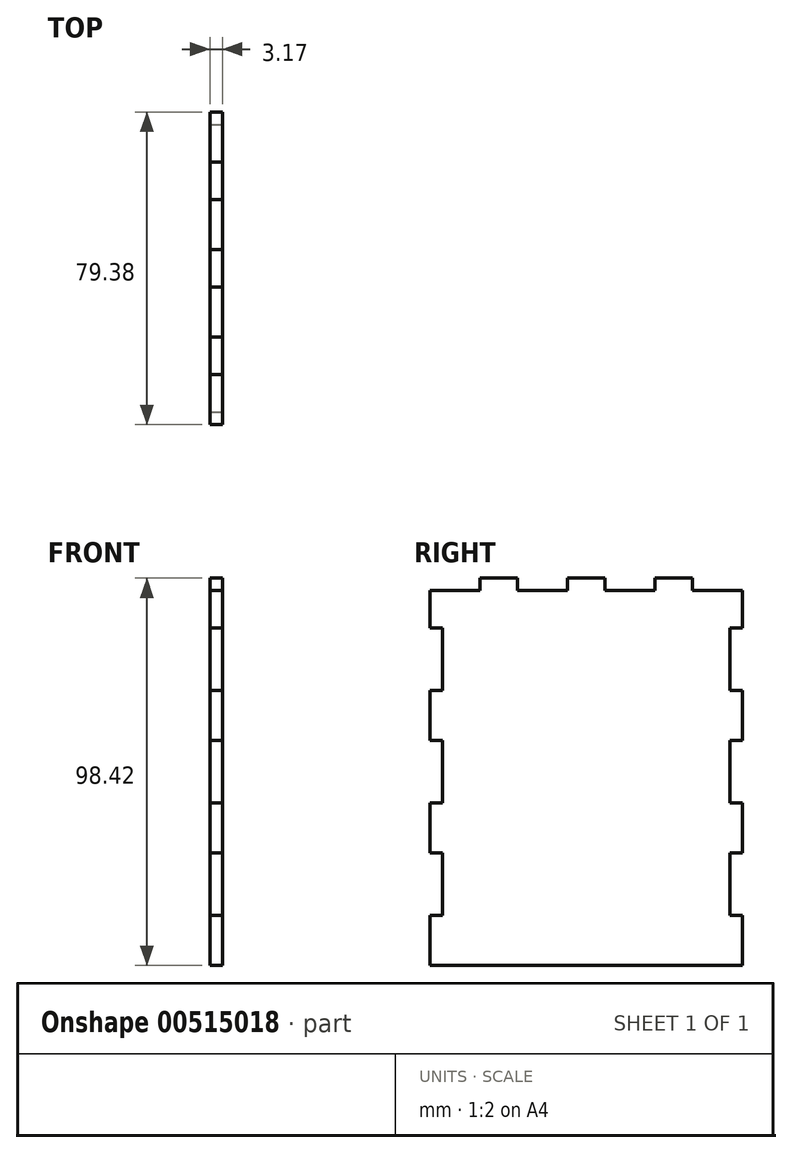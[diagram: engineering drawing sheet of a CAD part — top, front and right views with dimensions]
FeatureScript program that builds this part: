
annotation { "Feature Type Name" : "Feature", "Feature Type Description" : "" }
export const myFeature = defineFeature(function(context is Context, id is Id, definition is map)
    precondition{}
    {
        {
            var Q0;
            Q0=qCreatedBy(makeId("Right.planeOp"),FACE);
            var sketch = newSketch(context, id + "F0", { "sketchPlane" : qUnion([Q0])});
            skLineSegment(sketch, "E0.bottom", {"start": v(-39.69, 49.21) * mm, "end": v(39.69, 49.21) * mm});
            skLineSegment(sketch, "E0.top", {"start": v(-39.69, -49.21) * mm, "end": v(39.69, -49.21) * mm});
            skLineSegment(sketch, "E0.left", {"start": v(-39.69, 49.21) * mm, "end": v(-39.69, -49.21) * mm});
            skLineSegment(sketch, "E0.right", {"start": v(39.69, 49.21) * mm, "end": v(39.69, -49.21) * mm});
            skSolve(sketch);
        }
        {
            var Q0;
            Q0 = qSketchRegion(id + "F0", true);
            extrude(context, id + "F1", {"entities" : qUnion([Q0]), "depth" : 3.17 * mm, "offsetDistance" : 25.4 * mm});
        }
        {
            var Q0;
            Q0=makeQuery(id+"F1.opExtrude","CAP_FACE",FACE,{"disambiguationData":[OSD([sQuery(id+"F0.wireOp",EDGE,"E0.bottom"),sQuery(id+"F0.wireOp",EDGE,"E0.top"),sQuery(id+"F0.wireOp",EDGE,"E0.left"),sQuery(id+"F0.wireOp",EDGE,"E0.right")])],"isStart":false});
            var sketch = newSketch(context, id + "F2", { "sketchPlane" : qUnion([Q0])});
            skLineSegment(sketch, "E1", {"start": v(0, 49.21) * mm, "end": v(0, -49.21) * mm, "construction": true});
            skLineSegment(sketch, "E2.bottom", {"start": v(-39.69, 36.51) * mm, "end": v(-36.51, 36.51) * mm});
            skLineSegment(sketch, "E2.top", {"start": v(-39.69, 20.64) * mm, "end": v(-36.51, 20.64) * mm});
            skLineSegment(sketch, "E2.left", {"start": v(-39.69, 36.51) * mm, "end": v(-39.69, 20.64) * mm});
            skLineSegment(sketch, "E2.right", {"start": v(-36.51, 36.51) * mm, "end": v(-36.51, 20.64) * mm});
            skLineSegment(sketch, "E3.0.1.0", {"start": v(-39.69, -7.94) * mm, "end": v(-36.51, -7.94) * mm});
            skLineSegment(sketch, "E3.0.1.1", {"start": v(-39.69, 7.94) * mm, "end": v(-39.69, -7.94) * mm});
            skLineSegment(sketch, "E3.0.1.2", {"start": v(-39.69, 7.94) * mm, "end": v(-36.51, 7.94) * mm});
            skLineSegment(sketch, "E3.0.1.3", {"start": v(-36.51, 7.94) * mm, "end": v(-36.51, -7.94) * mm});
            skLineSegment(sketch, "E3.0.2.0", {"start": v(-39.69, -36.51) * mm, "end": v(-36.51, -36.51) * mm});
            skLineSegment(sketch, "E3.0.2.1", {"start": v(-39.69, -20.64) * mm, "end": v(-39.69, -36.51) * mm});
            skLineSegment(sketch, "E3.0.2.2", {"start": v(-39.69, -20.64) * mm, "end": v(-36.51, -20.64) * mm});
            skLineSegment(sketch, "E3.0.2.3", {"start": v(-36.51, -20.64) * mm, "end": v(-36.51, -36.51) * mm});
            skLineSegment(sketch, "E3.direction1", {"start": v(-39.69, 20.64) * mm, "end": v(-14.29, 20.64) * mm, "construction": true});
            skLineSegment(sketch, "E3.direction2", {"start": v(-39.69, 20.64) * mm, "end": v(-39.69, -7.94) * mm, "construction": true});
            skLineSegment(sketch, "E4.MirrorCS", {"start": v(39.69, 20.64) * mm, "end": v(36.51, 20.64) * mm});
            skLineSegment(sketch, "E5.MirrorCS", {"start": v(39.69, -36.51) * mm, "end": v(36.51, -36.51) * mm});
            skLineSegment(sketch, "E6.MirrorCS", {"start": v(39.69, -20.64) * mm, "end": v(36.51, -20.64) * mm});
            skLineSegment(sketch, "E7.MirrorCS", {"start": v(39.69, -7.94) * mm, "end": v(36.51, -7.94) * mm});
            skLineSegment(sketch, "E8.MirrorCS", {"start": v(39.69, 36.51) * mm, "end": v(36.51, 36.51) * mm});
            skLineSegment(sketch, "E9.MirrorCS", {"start": v(39.69, 7.94) * mm, "end": v(36.51, 7.94) * mm});
            skLineSegment(sketch, "E10.MirrorCS", {"start": v(39.69, 7.94) * mm, "end": v(39.69, -7.94) * mm});
            skLineSegment(sketch, "E11.MirrorCS", {"start": v(39.69, 36.51) * mm, "end": v(39.69, 20.64) * mm});
            skLineSegment(sketch, "E12.MirrorCS", {"start": v(36.51, -20.64) * mm, "end": v(36.51, -36.51) * mm});
            skLineSegment(sketch, "E13.MirrorCS", {"start": v(39.69, 20.64) * mm, "end": v(39.69, -7.94) * mm, "construction": true});
            skLineSegment(sketch, "E14.MirrorCS", {"start": v(39.69, 20.64) * mm, "end": v(14.29, 20.64) * mm, "construction": true});
            skLineSegment(sketch, "E15.MirrorCS", {"start": v(36.51, 36.51) * mm, "end": v(36.51, 20.64) * mm});
            skLineSegment(sketch, "E16.MirrorCS", {"start": v(39.69, -20.64) * mm, "end": v(39.69, -36.51) * mm});
            skLineSegment(sketch, "E17.MirrorCS", {"start": v(36.51, 7.94) * mm, "end": v(36.51, -7.94) * mm});
            skSolve(sketch);
        }
        {
            var Q0;
            Q0 = qSketchRegion(id + "F2", true);
            extrude(context, id + "F3", {"entities" : qUnion([Q0]), "operationType" : NewBodyOperationType.REMOVE, "endBound" : BoundingType.THROUGH_ALL, "oppositeDirection" : true, "depth" : 25.4 * mm, "offsetDistance" : 25.4 * mm});
        }
        {
            var Q0;
            Q0=makeQuery(id+"F1.opExtrude","CAP_FACE",FACE,{"disambiguationData":[OSD([sQuery(id+"F0.wireOp",EDGE,"E0.bottom"),sQuery(id+"F0.wireOp",EDGE,"E0.top"),sQuery(id+"F0.wireOp",EDGE,"E0.left"),sQuery(id+"F0.wireOp",EDGE,"E0.right")])],"isStart":false});
            var sketch = newSketch(context, id + "F4", { "sketchPlane" : qUnion([Q0])});
            skLineSegment(sketch, "E18.bottom", {"start": v(-39.69, 49.21) * mm, "end": v(-26.99, 49.21) * mm});
            skLineSegment(sketch, "E18.top", {"start": v(-39.69, 46.04) * mm, "end": v(-26.99, 46.04) * mm});
            skLineSegment(sketch, "E18.left", {"start": v(-39.69, 49.21) * mm, "end": v(-39.69, 46.04) * mm});
            skLineSegment(sketch, "E18.right", {"start": v(-26.99, 49.21) * mm, "end": v(-26.99, 46.04) * mm});
            skLineSegment(sketch, "E19.1.0.0", {"start": v(-4.76, 49.21) * mm, "end": v(-4.76, 46.04) * mm});
            skLineSegment(sketch, "E19.1.0.1", {"start": v(-17.46, 49.21) * mm, "end": v(-17.46, 46.04) * mm});
            skLineSegment(sketch, "E19.1.0.2", {"start": v(-17.46, 46.04) * mm, "end": v(-4.76, 46.04) * mm});
            skLineSegment(sketch, "E19.1.0.3", {"start": v(-17.46, 49.21) * mm, "end": v(-4.76, 49.21) * mm});
            skLineSegment(sketch, "E19.2.0.0", {"start": v(17.46, 49.21) * mm, "end": v(17.46, 46.04) * mm});
            skLineSegment(sketch, "E19.2.0.1", {"start": v(4.76, 49.21) * mm, "end": v(4.76, 46.04) * mm});
            skLineSegment(sketch, "E19.2.0.2", {"start": v(4.76, 46.04) * mm, "end": v(17.46, 46.04) * mm});
            skLineSegment(sketch, "E19.2.0.3", {"start": v(4.76, 49.21) * mm, "end": v(17.46, 49.21) * mm});
            skLineSegment(sketch, "E19.3.0.0", {"start": v(39.69, 49.21) * mm, "end": v(39.69, 46.04) * mm});
            skLineSegment(sketch, "E19.3.0.1", {"start": v(26.99, 49.21) * mm, "end": v(26.99, 46.04) * mm});
            skLineSegment(sketch, "E19.3.0.2", {"start": v(26.99, 46.04) * mm, "end": v(39.69, 46.04) * mm});
            skLineSegment(sketch, "E19.3.0.3", {"start": v(26.99, 49.21) * mm, "end": v(39.69, 49.21) * mm});
            skLineSegment(sketch, "E19.direction1", {"start": v(-39.69, 46.04) * mm, "end": v(-17.46, 46.04) * mm, "construction": true});
            skSolve(sketch);
        }
        {
            var Q0;
            Q0 = qSketchRegion(id + "F4", true);
            extrude(context, id + "F5", {"entities" : qUnion([Q0]), "operationType" : NewBodyOperationType.REMOVE, "endBound" : BoundingType.THROUGH_ALL, "oppositeDirection" : true, "depth" : 25.4 * mm, "offsetDistance" : 25.4 * mm});
        }
    });
